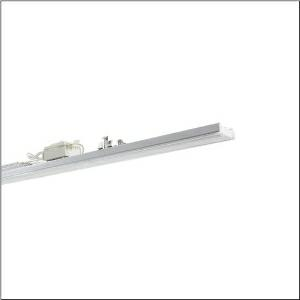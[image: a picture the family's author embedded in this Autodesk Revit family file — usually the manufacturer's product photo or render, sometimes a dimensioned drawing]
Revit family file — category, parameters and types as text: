
# Revit family: licross_r__21_recessed_ho_52tl12cn4c5m_6852
name_source: partatom
category: Lighting Fixtures
units: mm (PartAtom-declared; Revit-internal decimal feet)

## family parameters
Cut with Voids When Loaded = No
Host = Face
Light Source = No
Part Type = Normal
Room Calculation Point = No
Round Connector Dimension = Use Diameter
Shared = No

## types (1)
- --- (1 x LED, 12670 lm, 68.4 W, 4000K)
    Apparent Load = 68 VA
    CIE Flux Codes = 69 91 98 100 100
    Color Rendering = 80
    Color Temperature = 4000K
    Default Elevation = 1800 mm
    Description = Licross® 21 Recessed HO, luminaire insert, of sheet steel, galvanised, coil coated, white, length: 1.500mm, width: 66mm, height: 67mm, LED rated luminous flux: 12.670lm, light colour: 840, control gear: ON/OFF Multilumen, CLOi, control gear: ECG Multilumen, with plug, 3-pole, with phase selection, mains connection: 220..240V, AC, 50/60Hz, start of lifetime: 68W, end of service life: 83W, halogen-free wiring, primary optical cover: cover, of PMMA, light emission: direct distribution, primary light characteristic: symmetric, protection rating (complete): IP40, insulation class (complete): insulation class I (protective earthing), certification: CE, ENEC, VDE, UKCA, protection symbol: D if used in an environment without relevant dust loads with corresponding accessories, impact resistance: IK06, permissible ambient temperature for indoor applications: -35..+30°C, corresponds to IFS (International Featured Standards) requirements for safety and quality in the food industry, reducing of maximum allowable ambient temperature of 5°C with ceiling mounting, LABS conformity tested according to VDMA 24364:2018-05, packaging unit: 1 piece
    Height = 58 mm
    Lamp = 1 x LED
    Lamp Light Flux = 12670 lm
    Lamp Power = 68.4 W
    Lamp count = 1
    Length = 1500 mm
    Luminous efficacy = 185 lm/W
    Manufacturer = Siteco
    ModVariant = No
    Model = 52TL12CN4C5M
    Mounting Place = Ceiling
    Mounting Type = Pendant
    Number of Poles = 1
    OnlyDefault = Yes
    Power Factor = 1
    Product Name = Licross® 21 Recessed HO
    Product group = luminaire insert
    ProductGroupID = 902
    Protection Class = Protection class I
    Protection Degree = IP 40
    RLX_Detail_Level = 1
    RLX_Emergency_Light_Flux = 0 lm
    RLX_Emergency_Type = 0
    RLX_Emergency_Type_DB = No
    RlxData = <blob elided: 22341 chars, md5=213c5b2d>
    Socket = socket
    Standby Power = 0 W
    System Light Flux = 12670 lm
    System Power = 68 W
    Type Comments = factory setting: luminous flux: 100 % | (A | C | E) | 161 mA
    Type Image = l_1296930.jpg
    URL = http://relux.com
    VarID = @adj_109874
    Voltage = 0 V
    Weight = 0.00 kg
    Width = 66 mm

## geometry (parser evidence)
native form markers: Blend x4, Sweep x11
no freeform markers — native parametric forms only
